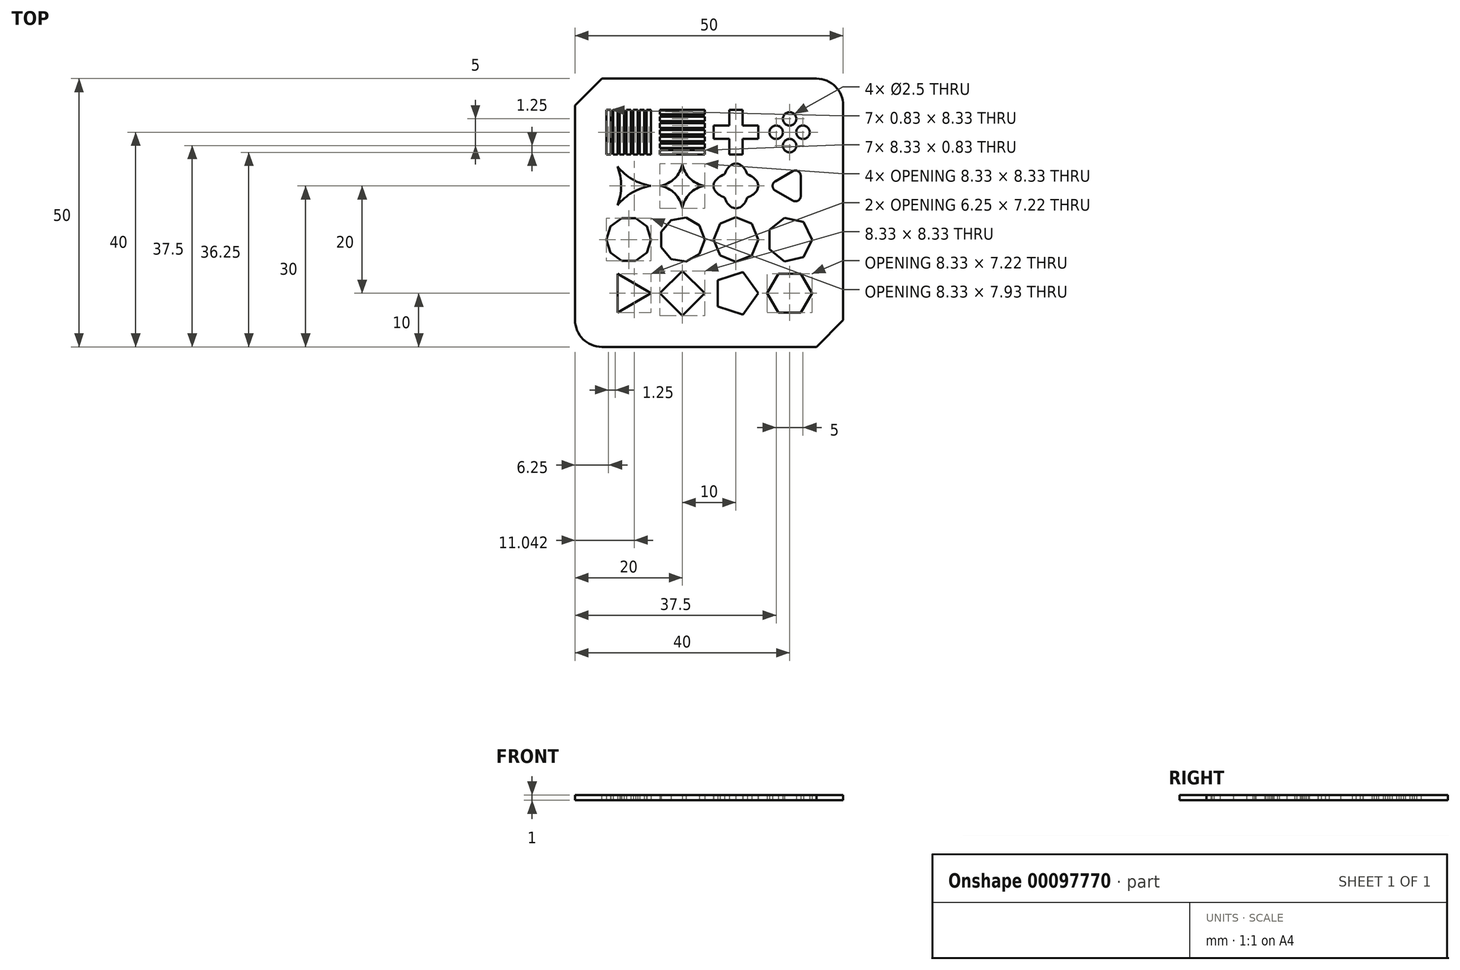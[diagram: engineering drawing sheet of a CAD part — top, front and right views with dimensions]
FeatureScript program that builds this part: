
annotation { "Feature Type Name" : "Feature", "Feature Type Description" : "" }
export const myFeature = defineFeature(function(context is Context, id is Id, definition is map)
    precondition{}
    {
        {
            assignVariable(context, id + "F0", {"name" : "Size", "anyValue" : 50});
        }
        {
            var Q0;
            Q0=qCreatedBy(makeId("Top.planeOp"),FACE);
            var sketch = newSketch(context, id + "F1", { "sketchPlane" : qUnion([Q0])});
            skLineSegment(sketch, "E0.bottom", {"start": v(25, -25) * mm, "end": v(-25, -25) * mm});
            skLineSegment(sketch, "E0.top", {"start": v(25, 25) * mm, "end": v(-25, 25) * mm});
            skLineSegment(sketch, "E0.left", {"start": v(25, -25) * mm, "end": v(25, 25) * mm});
            skLineSegment(sketch, "E0.right", {"start": v(-25, -25) * mm, "end": v(-25, 25) * mm});
            skPoint(sketch, "E0.middle", {"position": v(0, 0) * mm});
            skLineSegment(sketch, "E1.0.1.0", {"start": v(25, 15) * mm, "end": v(-25, 15) * mm, "construction": true});
            skLineSegment(sketch, "E1.0.2.0", {"start": v(25, 5) * mm, "end": v(-25, 5) * mm, "construction": true});
            skLineSegment(sketch, "E1.0.3.0", {"start": v(25, -5) * mm, "end": v(-25, -5) * mm, "construction": true});
            skLineSegment(sketch, "E1.0.4.0", {"start": v(25, -15) * mm, "end": v(-25, -15) * mm, "construction": true});
            skLineSegment(sketch, "E1.direction1", {"start": v(-67.36, 25) * mm, "end": v(-25, 25) * mm, "construction": true});
            skLineSegment(sketch, "E1.direction2", {"start": v(-25, 25) * mm, "end": v(-25, 15) * mm, "construction": true});
            skLineSegment(sketch, "E2.1.0.0", {"start": v(-15, -25) * mm, "end": v(-15, 25) * mm, "construction": true});
            skLineSegment(sketch, "E2.2.0.0", {"start": v(-5, -25) * mm, "end": v(-5, 25) * mm, "construction": true});
            skLineSegment(sketch, "E2.3.0.0", {"start": v(5, -25) * mm, "end": v(5, 25) * mm, "construction": true});
            skLineSegment(sketch, "E2.4.0.0", {"start": v(15, -25) * mm, "end": v(15, 25) * mm, "construction": true});
            skLineSegment(sketch, "E2.direction1", {"start": v(-25, -25) * mm, "end": v(-15, -25) * mm, "construction": true});
            skCircle(sketch, "E3.cCircle", {"center": v(-15, -15) * mm, "radius": 4.17 * mm, "construction": true});
            skLineSegment(sketch, "E3.0", {"start": v(-10.83, -15) * mm, "end": v(-17.08, -18.6) * mm});
            skLineSegment(sketch, "E3.1", {"start": v(-17.08, -18.6) * mm, "end": v(-17.08, -11.4) * mm});
            skLineSegment(sketch, "E3.2", {"start": v(-17.08, -11.4) * mm, "end": v(-10.83, -15) * mm});
            skCircle(sketch, "E4.cCircle", {"center": v(-5, -15) * mm, "radius": 4.17 * mm, "construction": true});
            skLineSegment(sketch, "E4.0", {"start": v(-0.83, -15) * mm, "end": v(-5, -19.17) * mm});
            skLineSegment(sketch, "E4.1", {"start": v(-5, -19.17) * mm, "end": v(-9.17, -15) * mm});
            skLineSegment(sketch, "E4.2", {"start": v(-9.17, -15) * mm, "end": v(-5, -10.83) * mm});
            skLineSegment(sketch, "E4.3", {"start": v(-5, -10.83) * mm, "end": v(-0.83, -15) * mm});
            skCircle(sketch, "E5.cCircle", {"center": v(5, -15) * mm, "radius": 4.17 * mm, "construction": true});
            skLineSegment(sketch, "E5.0", {"start": v(9.17, -15) * mm, "end": v(6.29, -18.96) * mm});
            skLineSegment(sketch, "E5.1", {"start": v(6.29, -18.96) * mm, "end": v(1.63, -17.45) * mm});
            skLineSegment(sketch, "E5.2", {"start": v(1.63, -17.45) * mm, "end": v(1.63, -12.55) * mm});
            skLineSegment(sketch, "E5.3", {"start": v(1.63, -12.55) * mm, "end": v(6.29, -11.04) * mm});
            skLineSegment(sketch, "E5.4", {"start": v(6.29, -11.04) * mm, "end": v(9.17, -15) * mm});
            skCircle(sketch, "E6.cCircle", {"center": v(15, -15) * mm, "radius": 4.17 * mm, "construction": true});
            skLineSegment(sketch, "E6.0", {"start": v(19.17, -15) * mm, "end": v(17.08, -18.6) * mm});
            skLineSegment(sketch, "E6.1", {"start": v(17.08, -18.6) * mm, "end": v(12.92, -18.6) * mm});
            skLineSegment(sketch, "E6.2", {"start": v(12.92, -18.6) * mm, "end": v(10.83, -15) * mm});
            skLineSegment(sketch, "E6.3", {"start": v(10.83, -15) * mm, "end": v(12.92, -11.4) * mm});
            skLineSegment(sketch, "E6.4", {"start": v(12.92, -11.4) * mm, "end": v(17.08, -11.4) * mm});
            skLineSegment(sketch, "E6.5", {"start": v(17.08, -11.4) * mm, "end": v(19.17, -15) * mm});
            skCircle(sketch, "E7.cCircle", {"center": v(15, -5) * mm, "radius": 4.17 * mm, "construction": true});
            skLineSegment(sketch, "E7.0", {"start": v(19.17, -5) * mm, "end": v(17.6, -8.26) * mm});
            skLineSegment(sketch, "E7.1", {"start": v(17.6, -8.26) * mm, "end": v(14.07, -9.06) * mm});
            skLineSegment(sketch, "E7.2", {"start": v(14.07, -9.06) * mm, "end": v(11.25, -6.8) * mm});
            skLineSegment(sketch, "E7.3", {"start": v(11.25, -6.8) * mm, "end": v(11.25, -3.2) * mm});
            skLineSegment(sketch, "E7.4", {"start": v(11.25, -3.2) * mm, "end": v(14.07, -0.94) * mm});
            skLineSegment(sketch, "E7.5", {"start": v(14.07, -0.94) * mm, "end": v(17.6, -1.74) * mm});
            skLineSegment(sketch, "E7.6", {"start": v(17.6, -1.74) * mm, "end": v(19.17, -5) * mm});
            skCircle(sketch, "E8.cCircle", {"center": v(5, -5) * mm, "radius": 4.17 * mm, "construction": true});
            skLineSegment(sketch, "E8.0", {"start": v(9.17, -5) * mm, "end": v(7.95, -7.95) * mm});
            skLineSegment(sketch, "E8.1", {"start": v(7.95, -7.95) * mm, "end": v(5, -9.17) * mm});
            skLineSegment(sketch, "E8.2", {"start": v(5, -9.17) * mm, "end": v(2.05, -7.95) * mm});
            skLineSegment(sketch, "E8.3", {"start": v(2.05, -7.95) * mm, "end": v(0.83, -5) * mm});
            skLineSegment(sketch, "E8.4", {"start": v(0.83, -5) * mm, "end": v(2.05, -2.05) * mm});
            skLineSegment(sketch, "E8.5", {"start": v(2.05, -2.05) * mm, "end": v(5, -0.83) * mm});
            skLineSegment(sketch, "E8.6", {"start": v(5, -0.83) * mm, "end": v(7.95, -2.05) * mm});
            skLineSegment(sketch, "E8.7", {"start": v(7.95, -2.05) * mm, "end": v(9.17, -5) * mm});
            skCircle(sketch, "E9.cCircle", {"center": v(-5, -5) * mm, "radius": 4.17 * mm, "construction": true});
            skLineSegment(sketch, "E9.0", {"start": v(-0.83, -5) * mm, "end": v(-1.8, -7.68) * mm});
            skLineSegment(sketch, "E9.1", {"start": v(-1.8, -7.68) * mm, "end": v(-4.28, -9.1) * mm});
            skLineSegment(sketch, "E9.2", {"start": v(-4.28, -9.1) * mm, "end": v(-7.08, -8.6) * mm});
            skLineSegment(sketch, "E9.3", {"start": v(-7.08, -8.6) * mm, "end": v(-8.92, -6.43) * mm});
            skLineSegment(sketch, "E9.4", {"start": v(-8.92, -6.43) * mm, "end": v(-8.92, -3.57) * mm});
            skLineSegment(sketch, "E9.5", {"start": v(-8.92, -3.57) * mm, "end": v(-7.08, -1.4) * mm});
            skLineSegment(sketch, "E9.6", {"start": v(-7.08, -1.4) * mm, "end": v(-4.28, -0.9) * mm});
            skLineSegment(sketch, "E9.7", {"start": v(-4.28, -0.9) * mm, "end": v(-1.8, -2.32) * mm});
            skLineSegment(sketch, "E9.8", {"start": v(-1.8, -2.32) * mm, "end": v(-0.83, -5) * mm});
            skCircle(sketch, "E10.cCircle", {"center": v(-15, -5) * mm, "radius": 4.17 * mm, "construction": true});
            skLineSegment(sketch, "E10.0", {"start": v(-10.83, -5) * mm, "end": v(-11.63, -7.45) * mm});
            skLineSegment(sketch, "E10.1", {"start": v(-11.63, -7.45) * mm, "end": v(-13.71, -8.96) * mm});
            skLineSegment(sketch, "E10.2", {"start": v(-13.71, -8.96) * mm, "end": v(-16.29, -8.96) * mm});
            skLineSegment(sketch, "E10.3", {"start": v(-16.29, -8.96) * mm, "end": v(-18.37, -7.45) * mm});
            skLineSegment(sketch, "E10.4", {"start": v(-18.37, -7.45) * mm, "end": v(-19.17, -5) * mm});
            skLineSegment(sketch, "E10.5", {"start": v(-19.17, -5) * mm, "end": v(-18.37, -2.55) * mm});
            skLineSegment(sketch, "E10.6", {"start": v(-18.37, -2.55) * mm, "end": v(-16.29, -1.04) * mm});
            skLineSegment(sketch, "E10.7", {"start": v(-16.29, -1.04) * mm, "end": v(-13.71, -1.04) * mm});
            skLineSegment(sketch, "E10.8", {"start": v(-13.71, -1.04) * mm, "end": v(-11.63, -2.55) * mm});
            skLineSegment(sketch, "E10.9", {"start": v(-11.63, -2.55) * mm, "end": v(-10.83, -5) * mm});
            skCircle(sketch, "E11.cCircle", {"center": v(-15, 5) * mm, "radius": 4.17 * mm, "construction": true});
            skCircle(sketch, "E12.cCircle", {"center": v(-5, 5) * mm, "radius": 4.17 * mm, "construction": true});
            skArc(sketch, "E13", {"start": v(-9.17, 5) * mm, "mid": v(-6.4, 6.4) * mm, "end": v(-5, 9.17) * mm});
            skArc(sketch, "E14", {"start": v(-0.83, 5) * mm, "mid": v(-3.6, 3.6) * mm, "end": v(-5, 0.83) * mm});
            skArc(sketch, "E15", {"start": v(-5, 9.17) * mm, "mid": v(-3.6, 6.4) * mm, "end": v(-0.83, 5) * mm});
            skArc(sketch, "E16", {"start": v(-5, 0.83) * mm, "mid": v(-6.4, 3.6) * mm, "end": v(-9.17, 5) * mm});
            skArc(sketch, "E17", {"start": v(-17.08, 1.4) * mm, "mid": v(-16.4, 5) * mm, "end": v(-17.08, 8.6) * mm});
            skArc(sketch, "E18", {"start": v(-17.08, 8.6) * mm, "mid": v(-14.3, 6.22) * mm, "end": v(-10.83, 5) * mm});
            skArc(sketch, "E19", {"start": v(-10.83, 5) * mm, "mid": v(-14.3, 3.78) * mm, "end": v(-17.08, 1.4) * mm});
            skCircle(sketch, "E20", {"center": v(5, 5) * mm, "radius": 4.17 * mm, "construction": true});
            skCircle(sketch, "E21.cCircle", {"center": v(15, 5) * mm, "radius": 4.17 * mm, "construction": true});
            skLineSegment(sketch, "E21.0", {"start": v(12.33, 5.87) * mm, "end": v(15.58, 7.74) * mm});
            skLineSegment(sketch, "E21.1", {"start": v(17.08, 6.88) * mm, "end": v(17.08, 3.12) * mm});
            skLineSegment(sketch, "E21.2", {"start": v(15.58, 2.26) * mm, "end": v(12.33, 4.13) * mm});
            skPoint(sketch, "E22.visualSharp", {"position": v(10.83, 5) * mm});
            skArc(sketch, "E22.filletArc", {"start": v(12.33, 5.87) * mm, "mid": v(11.83, 5) * mm, "end": v(12.33, 4.13) * mm});
            skPoint(sketch, "E23.visualSharp", {"position": v(17.08, 1.4) * mm});
            skArc(sketch, "E23.filletArc", {"start": v(15.58, 2.26) * mm, "mid": v(16.58, 2.26) * mm, "end": v(17.08, 3.12) * mm});
            skPoint(sketch, "E24.visualSharp", {"position": v(17.08, 8.6) * mm});
            skArc(sketch, "E24.filletArc", {"start": v(17.08, 6.88) * mm, "mid": v(16.58, 7.74) * mm, "end": v(15.58, 7.74) * mm});
            skEllipse(sketch, "E25", {"center": v(5, 5) * mm, "majorRadius": 4.17 * mm, "minorRadius": 2.5 * mm, "majorAxis": v(0, 1)});
            skEllipse(sketch, "E26", {"center": v(5, 5) * mm, "majorRadius": 4.17 * mm, "minorRadius": 2.5 * mm, "majorAxis": v(1, 0)});
            skLineSegment(sketch, "E27.bottom", {"start": v(3.75, 19.17) * mm, "end": v(6.25, 19.17) * mm});
            skLineSegment(sketch, "E27.top", {"start": v(3.75, 10.83) * mm, "end": v(6.25, 10.83) * mm});
            skLineSegment(sketch, "E27.left", {"start": v(3.75, 19.17) * mm, "end": v(3.75, 10.83) * mm});
            skLineSegment(sketch, "E27.right", {"start": v(6.25, 19.17) * mm, "end": v(6.25, 10.83) * mm});
            skPoint(sketch, "E27.middle", {"position": v(5, 15) * mm});
            skLineSegment(sketch, "E28.bottom", {"start": v(9.17, 13.75) * mm, "end": v(0.83, 13.75) * mm});
            skLineSegment(sketch, "E28.top", {"start": v(9.17, 16.25) * mm, "end": v(0.83, 16.25) * mm});
            skLineSegment(sketch, "E28.left", {"start": v(9.17, 13.75) * mm, "end": v(9.17, 16.25) * mm});
            skLineSegment(sketch, "E28.right", {"start": v(0.83, 13.75) * mm, "end": v(0.83, 16.25) * mm});
            skCircle(sketch, "E29", {"center": v(15, 15) * mm, "radius": 2.5 * mm, "construction": true});
            skCircle(sketch, "E30", {"center": v(15, 17.5) * mm, "radius": 1.25 * mm});
            skCircle(sketch, "E31.1.0", {"center": v(12.5, 15) * mm, "radius": 1.25 * mm});
            skCircle(sketch, "E31.2.0", {"center": v(15, 12.5) * mm, "radius": 1.25 * mm});
            skCircle(sketch, "E31.3.0", {"center": v(17.5, 15) * mm, "radius": 1.25 * mm});
            skLineSegment(sketch, "E32.left", {"start": v(-0.83, 10.83) * mm, "end": v(-0.83, 19.17) * mm, "construction": true});
            skLineSegment(sketch, "E32.right", {"start": v(-9.17, 10.83) * mm, "end": v(-9.17, 19.17) * mm, "construction": true});
            skPoint(sketch, "E32.middle", {"position": v(-5, 15) * mm});
            skLineSegment(sketch, "E33.bottom", {"start": v(-10.83, 10.83) * mm, "end": v(-19.17, 10.83) * mm, "construction": true});
            skLineSegment(sketch, "E33.top", {"start": v(-10.83, 19.17) * mm, "end": v(-19.17, 19.17) * mm, "construction": true});
            skLineSegment(sketch, "E33.right", {"start": v(-19.17, 10.83) * mm, "end": v(-19.17, 19.17) * mm});
            skPoint(sketch, "E33.middle", {"position": v(-15, 15) * mm});
            skLineSegment(sketch, "E34.bottom", {"start": v(-19.17, 19.17) * mm, "end": v(-18.33, 19.17) * mm});
            skLineSegment(sketch, "E34.top", {"start": v(-19.17, 10.83) * mm, "end": v(-18.33, 10.83) * mm});
            skLineSegment(sketch, "E34.left", {"start": v(-19.17, 19.17) * mm, "end": v(-19.17, 10.83) * mm});
            skLineSegment(sketch, "E34.right", {"start": v(-18.33, 19.17) * mm, "end": v(-18.33, 10.83) * mm});
            skLineSegment(sketch, "E35.1.0.0", {"start": v(-17.92, 19.17) * mm, "end": v(-17.92, 10.83) * mm});
            skLineSegment(sketch, "E35.1.0.1", {"start": v(-17.08, 19.17) * mm, "end": v(-17.08, 10.83) * mm});
            skLineSegment(sketch, "E35.1.0.2", {"start": v(-17.92, 19.17) * mm, "end": v(-17.08, 19.17) * mm});
            skLineSegment(sketch, "E35.1.0.3", {"start": v(-17.92, 10.83) * mm, "end": v(-17.08, 10.83) * mm});
            skLineSegment(sketch, "E35.2.0.0", {"start": v(-16.67, 19.17) * mm, "end": v(-16.67, 10.83) * mm});
            skLineSegment(sketch, "E35.2.0.1", {"start": v(-15.83, 19.17) * mm, "end": v(-15.83, 10.83) * mm});
            skLineSegment(sketch, "E35.2.0.2", {"start": v(-16.67, 19.17) * mm, "end": v(-15.83, 19.17) * mm});
            skLineSegment(sketch, "E35.2.0.3", {"start": v(-16.67, 10.83) * mm, "end": v(-15.83, 10.83) * mm});
            skLineSegment(sketch, "E35.3.0.0", {"start": v(-15.42, 19.17) * mm, "end": v(-15.42, 10.83) * mm});
            skLineSegment(sketch, "E35.3.0.1", {"start": v(-14.58, 19.17) * mm, "end": v(-14.58, 10.83) * mm});
            skLineSegment(sketch, "E35.3.0.2", {"start": v(-15.42, 19.17) * mm, "end": v(-14.58, 19.17) * mm});
            skLineSegment(sketch, "E35.3.0.3", {"start": v(-15.42, 10.83) * mm, "end": v(-14.58, 10.83) * mm});
            skLineSegment(sketch, "E35.4.0.0", {"start": v(-14.17, 19.17) * mm, "end": v(-14.17, 10.83) * mm});
            skLineSegment(sketch, "E35.4.0.1", {"start": v(-13.33, 19.17) * mm, "end": v(-13.33, 10.83) * mm});
            skLineSegment(sketch, "E35.4.0.2", {"start": v(-14.17, 19.17) * mm, "end": v(-13.33, 19.17) * mm});
            skLineSegment(sketch, "E35.4.0.3", {"start": v(-14.17, 10.83) * mm, "end": v(-13.33, 10.83) * mm});
            skLineSegment(sketch, "E35.5.0.0", {"start": v(-12.92, 19.17) * mm, "end": v(-12.92, 10.83) * mm});
            skLineSegment(sketch, "E35.5.0.1", {"start": v(-12.08, 19.17) * mm, "end": v(-12.08, 10.83) * mm});
            skLineSegment(sketch, "E35.5.0.2", {"start": v(-12.92, 19.17) * mm, "end": v(-12.08, 19.17) * mm});
            skLineSegment(sketch, "E35.5.0.3", {"start": v(-12.92, 10.83) * mm, "end": v(-12.08, 10.83) * mm});
            skLineSegment(sketch, "E35.6.0.0", {"start": v(-11.67, 19.17) * mm, "end": v(-11.67, 10.83) * mm});
            skLineSegment(sketch, "E35.6.0.1", {"start": v(-10.83, 19.17) * mm, "end": v(-10.83, 10.83) * mm});
            skLineSegment(sketch, "E35.6.0.2", {"start": v(-11.67, 19.17) * mm, "end": v(-10.83, 19.17) * mm});
            skLineSegment(sketch, "E35.6.0.3", {"start": v(-11.67, 10.83) * mm, "end": v(-10.83, 10.83) * mm});
            skLineSegment(sketch, "E35.direction1", {"start": v(-19.17, 10.83) * mm, "end": v(-17.92, 10.83) * mm, "construction": true});
            skLineSegment(sketch, "E36.bottom", {"start": v(-9.17, 19.17) * mm, "end": v(-0.83, 19.17) * mm});
            skLineSegment(sketch, "E36.top", {"start": v(-9.17, 18.33) * mm, "end": v(-0.83, 18.33) * mm});
            skLineSegment(sketch, "E36.left", {"start": v(-9.17, 19.17) * mm, "end": v(-9.17, 18.33) * mm});
            skLineSegment(sketch, "E36.right", {"start": v(-0.83, 19.17) * mm, "end": v(-0.83, 18.33) * mm});
            skLineSegment(sketch, "E37.0.1.0", {"start": v(-9.17, 17.92) * mm, "end": v(-9.17, 17.08) * mm});
            skLineSegment(sketch, "E37.0.1.1", {"start": v(-9.17, 17.92) * mm, "end": v(-0.83, 17.92) * mm});
            skLineSegment(sketch, "E37.0.1.2", {"start": v(-0.83, 17.92) * mm, "end": v(-0.83, 17.08) * mm});
            skLineSegment(sketch, "E37.0.1.3", {"start": v(-9.17, 17.08) * mm, "end": v(-0.83, 17.08) * mm});
            skLineSegment(sketch, "E37.0.2.0", {"start": v(-9.17, 16.67) * mm, "end": v(-9.17, 15.83) * mm});
            skLineSegment(sketch, "E37.0.2.1", {"start": v(-9.17, 16.67) * mm, "end": v(-0.83, 16.67) * mm});
            skLineSegment(sketch, "E37.0.2.2", {"start": v(-0.83, 16.67) * mm, "end": v(-0.83, 15.83) * mm});
            skLineSegment(sketch, "E37.0.2.3", {"start": v(-9.17, 15.83) * mm, "end": v(-0.83, 15.83) * mm});
            skLineSegment(sketch, "E37.0.3.0", {"start": v(-9.17, 15.42) * mm, "end": v(-9.17, 14.58) * mm});
            skLineSegment(sketch, "E37.0.3.1", {"start": v(-9.17, 15.42) * mm, "end": v(-0.83, 15.42) * mm});
            skLineSegment(sketch, "E37.0.3.2", {"start": v(-0.83, 15.42) * mm, "end": v(-0.83, 14.58) * mm});
            skLineSegment(sketch, "E37.0.3.3", {"start": v(-9.17, 14.58) * mm, "end": v(-0.83, 14.58) * mm});
            skLineSegment(sketch, "E37.0.4.0", {"start": v(-9.17, 14.17) * mm, "end": v(-9.17, 13.33) * mm});
            skLineSegment(sketch, "E37.0.4.1", {"start": v(-9.17, 14.17) * mm, "end": v(-0.83, 14.17) * mm});
            skLineSegment(sketch, "E37.0.4.2", {"start": v(-0.83, 14.17) * mm, "end": v(-0.83, 13.33) * mm});
            skLineSegment(sketch, "E37.0.4.3", {"start": v(-9.17, 13.33) * mm, "end": v(-0.83, 13.33) * mm});
            skLineSegment(sketch, "E37.0.5.0", {"start": v(-9.17, 12.92) * mm, "end": v(-9.17, 12.08) * mm});
            skLineSegment(sketch, "E37.0.5.1", {"start": v(-9.17, 12.92) * mm, "end": v(-0.83, 12.92) * mm});
            skLineSegment(sketch, "E37.0.5.2", {"start": v(-0.83, 12.92) * mm, "end": v(-0.83, 12.08) * mm});
            skLineSegment(sketch, "E37.0.5.3", {"start": v(-9.17, 12.08) * mm, "end": v(-0.83, 12.08) * mm});
            skLineSegment(sketch, "E37.0.6.0", {"start": v(-9.17, 11.67) * mm, "end": v(-9.17, 10.83) * mm});
            skLineSegment(sketch, "E37.0.6.1", {"start": v(-9.17, 11.67) * mm, "end": v(-0.83, 11.67) * mm});
            skLineSegment(sketch, "E37.0.6.2", {"start": v(-0.83, 11.67) * mm, "end": v(-0.83, 10.83) * mm});
            skLineSegment(sketch, "E37.0.6.3", {"start": v(-9.17, 10.83) * mm, "end": v(-0.83, 10.83) * mm});
            skLineSegment(sketch, "E37.direction1", {"start": v(-9.17, 18.33) * mm, "end": v(15.83, 18.33) * mm, "construction": true});
            skLineSegment(sketch, "E37.direction2", {"start": v(-9.17, 18.33) * mm, "end": v(-9.17, 17.08) * mm, "construction": true});
            skSolve(sketch);
        }
        {
            var Q0;
            Q0=makeQuery(id+"F1.imprint","IMPRINT",FACE,{"disambiguationData":[TD([[makeQuery(id+"F1.imprint","IMPRINT",EDGE,{"derivedFrom":sQuery(id+"F1.wireOp",EDGE,"E0.bottom")}),-1.0]])]});
            extrude(context, id + "F2", {"entities" : qUnion([Q0]), "depth" : 1 * mm});
        }
        {
            var Q0;
            Q0=makeQuery(id+"F2.opExtrude","SWEPT_EDGE",EDGE,{"disambiguationData":[OSD([sQuery(id+"F1.wireOp",EDGE,"E0.bottom"),sQuery(id+"F1.wireOp",EDGE,"E0.right")])]});
            var Q1;
            Q1=makeQuery(id+"F2.opExtrude","SWEPT_EDGE",EDGE,{"disambiguationData":[OSD([sQuery(id+"F1.wireOp",EDGE,"E0.top"),sQuery(id+"F1.wireOp",EDGE,"E0.left")])]});
            fillet(context, id + "F3", {"entities" : qUnion([Q0, Q1]), "radius" : (getVariable(context, 'Size') / 10) * mm, "tangentPropagation" : true, "allowEdgeOverflow" : false});
        }
        {
            var Q0;
            Q0=makeQuery(id+"F2.opExtrude","SWEPT_EDGE",EDGE,{"disambiguationData":[OSD([sQuery(id+"F1.wireOp",EDGE,"E0.bottom"),sQuery(id+"F1.wireOp",EDGE,"E0.left")])]});
            var Q1;
            Q1=makeQuery(id+"F2.opExtrude","SWEPT_EDGE",EDGE,{"disambiguationData":[OSD([sQuery(id+"F1.wireOp",EDGE,"E0.top"),sQuery(id+"F1.wireOp",EDGE,"E0.right")])]});
            chamfer(context, id + "F4", {"entities" : qUnion([Q0, Q1]), "width" : (getVariable(context, 'Size') / 10) * mm, "tangentPropagation" : true});
        }
    });
